# Revit family: raindance_e_360_air_1jet_overhead_shower_with_shower_arm_390_mm_ecosmart_26605000___
name_source: partatom
category: Plumbing Fixtures
revit_build: Autodesk Revit 2015 (Build: 20140903_1530(x64)
units: mm (PartAtom-declared; Revit-internal decimal feet)

## types (1)
- Chrome 000
    BIMobject category = Showers
    BOSUseNativeGeometries = 1
    Brand url = http://www.hansgrohe-int.com
    Date of publishing = 1/12/2016
    Default Elevation = 4' - 0"
    Design country = Germany
    EAN code = https://4011097754390
    Edition number = 1
    IFC Classification = Sanitary Terminal
    Installation instructions = https://pro.hansgrohe-int.com
    Manufacturer country = Germany
    Manufacturer name = Hansgrohe
    Masterformat 2014 Code = 22 41 23
    Masterformat 2014 Description = Residential Showers
    Material main = Chrome
    NBS Reference Code = 35-06-81
    NBS Reference Description = Shower Heads
    Nominal height = 0
    Nominal width = 0
    OmniClass Code = 23-31 17 19
    OmniClass Description = Shower Head Fixtures
    Product Guid = 5fb8cd98-cedb-475e-88c2-bce602449582
    Product SKU = 26605000
    Product data url = https://bimobject.com
    Product family = Raindance E
    Product group = Overhead showers
    Product url = https://pro.hansgrohe-int.com
    QR code = http://bimobject.com
    Technical description = https://pro.hansgrohe-int.com
    UNSPSC Code = 30181503
    Uniclass 1.4 Code = L7214
    Uniclass 1.4 Description = Showers
    Uniclass 2.0 Code = PR-35-06-81
    Uniclass 2.0 Description = Shower Heads
    Uniclass 2015 Code = Pr_40_20_87_76
    Uniclass 2015 Name = Shower heads
    Uniformat II Code = D2010
    Uniformat II Description = Plumbing Fixtures
    Weight Net (Kg) = 0

## geometry (parser evidence)
native form markers: Sweep x1
no freeform markers — native parametric forms only
